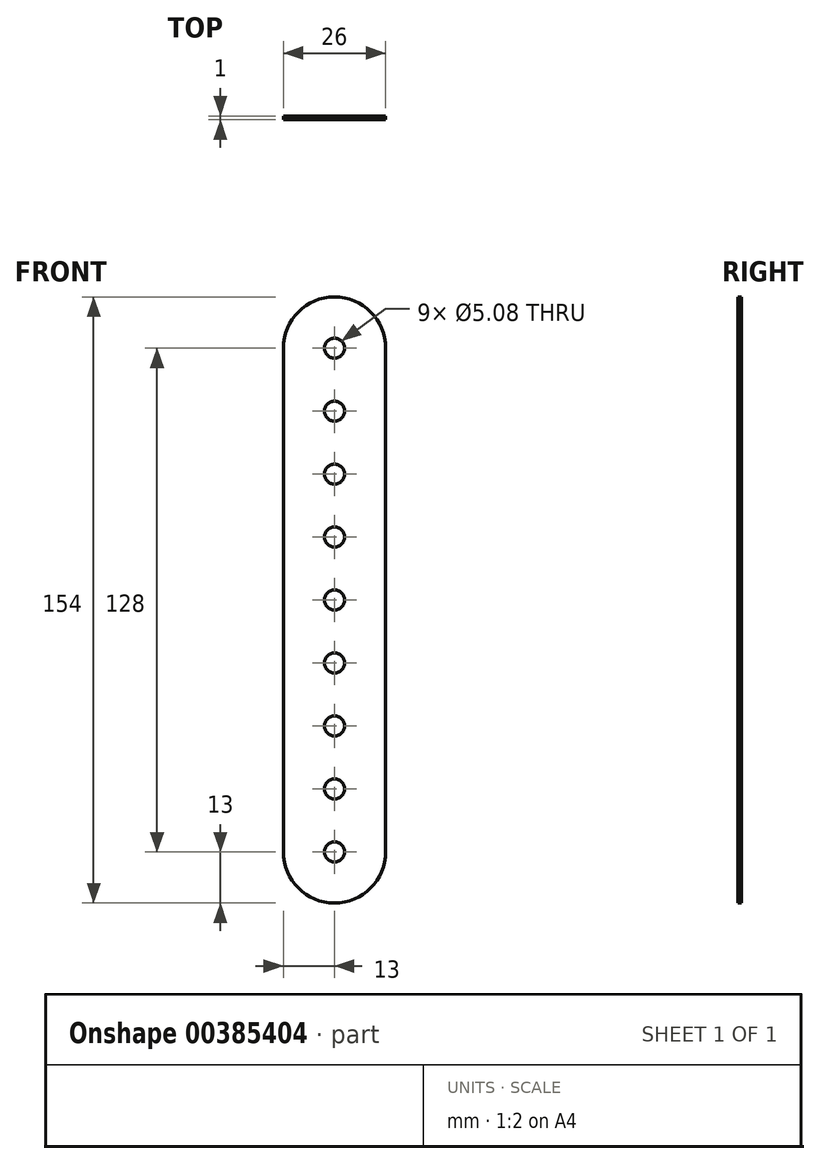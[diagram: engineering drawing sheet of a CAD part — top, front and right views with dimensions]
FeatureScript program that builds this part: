
annotation { "Feature Type Name" : "Feature", "Feature Type Description" : "" }
export const myFeature = defineFeature(function(context is Context, id is Id, definition is map)
    precondition{}
    {
        {
            var Q0;
            Q0=qCreatedBy(makeId("Front.planeOp"),FACE);
            var sketch = newSketch(context, id + "F0", { "sketchPlane" : qUnion([Q0])});
            skLineSegment(sketch, "E0", {"start": v(-13, 94.4) * mm, "end": v(-13, -33.6) * mm});
            skLineSegment(sketch, "E1", {"start": v(13, -33.6) * mm, "end": v(13, 94.4) * mm});
            skCircle(sketch, "E2", {"center": v(0, 94.4) * mm, "radius": 2.54 * mm});
            skCircle(sketch, "E3", {"center": v(0, -33.6) * mm, "radius": 2.54 * mm});
            skPoint(sketch, "E4", {"position": v(0, 78.4) * mm});
            skCircle(sketch, "E5", {"center": v(0, 78.4) * mm, "radius": 2.54 * mm});
            skCircle(sketch, "E6", {"center": v(0, 94.4) * mm, "radius": 13 * mm});
            skCircle(sketch, "E7", {"center": v(0, -33.6) * mm, "radius": 13 * mm});
            skCircle(sketch, "E8.0.1.0", {"center": v(0, -1.6) * mm, "radius": 2.54 * mm});
            skCircle(sketch, "E8.0.2.0", {"center": v(0, -17.6) * mm, "radius": 2.54 * mm});
            skCircle(sketch, "E9.0.1.0", {"center": v(0, 62.4) * mm, "radius": 2.54 * mm});
            skCircle(sketch, "E9.0.2.0", {"center": v(0, 46.4) * mm, "radius": 2.54 * mm});
            skCircle(sketch, "E9.0.3.0", {"center": v(0, 30.4) * mm, "radius": 2.54 * mm});
            skCircle(sketch, "E9.0.4.0", {"center": v(0, 14.4) * mm, "radius": 2.54 * mm});
            skSolve(sketch);
        }
        {
            var Q0;
            Q0=qSketchRegion(id+"F0",true);
            extrude(context, id + "F1", {"entities" : qUnion([Q0]), "depth" : 1 * mm});
        }
    });
